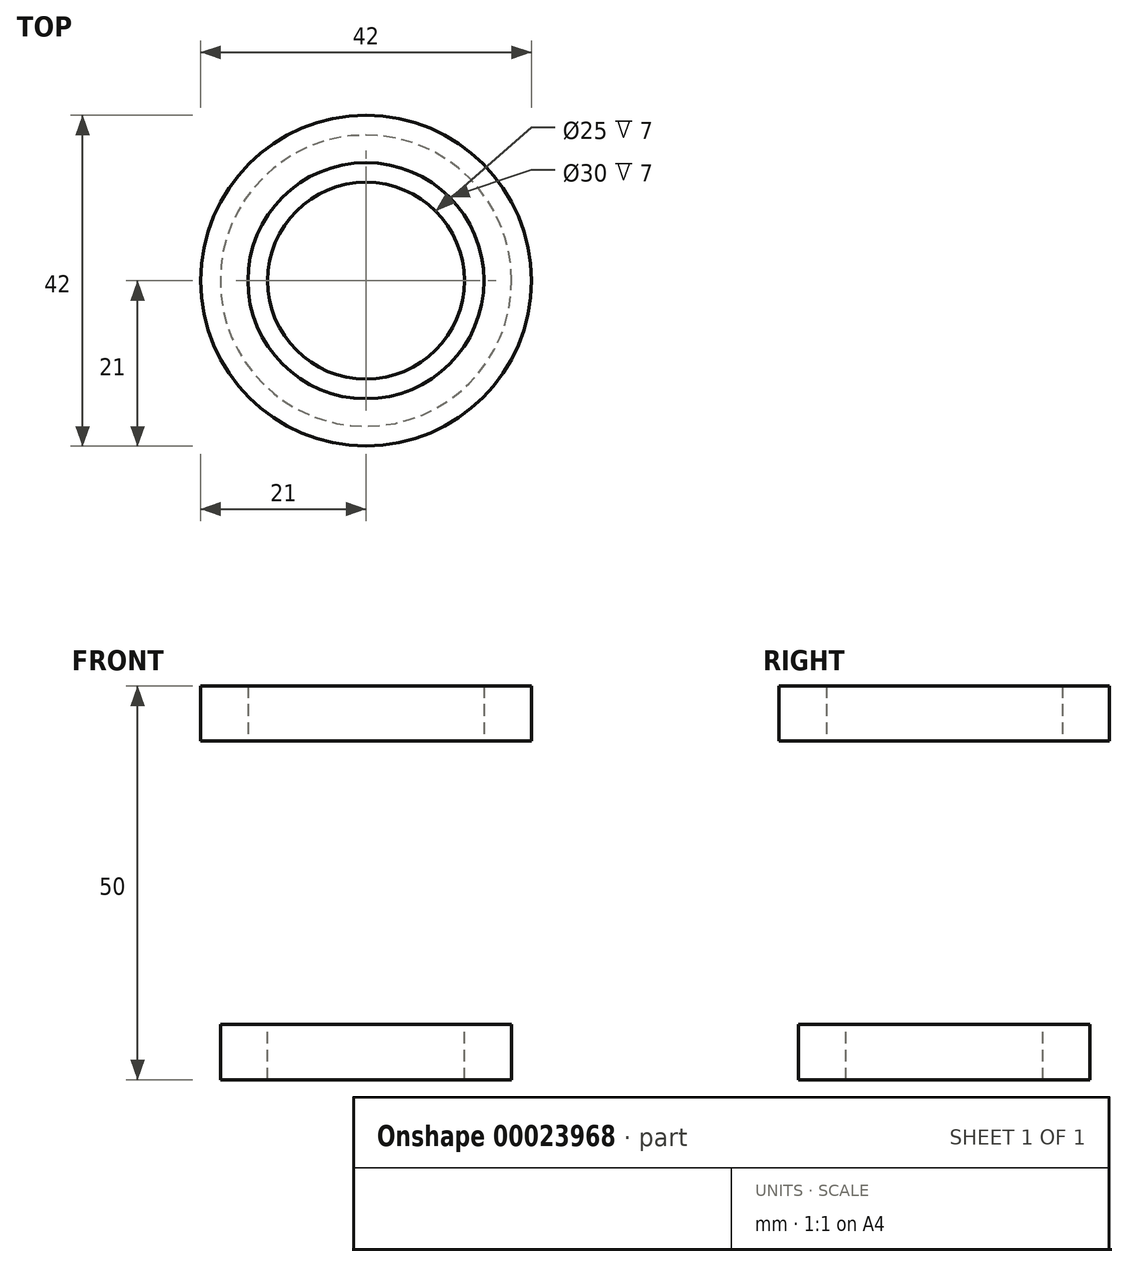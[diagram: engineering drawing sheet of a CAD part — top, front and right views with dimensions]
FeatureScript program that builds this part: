
annotation { "Feature Type Name" : "Feature", "Feature Type Description" : "" }
export const myFeature = defineFeature(function(context is Context, id is Id, definition is map)
    precondition{}
    {
        {
            var Q0;
            Q0=qCreatedBy(makeId("Front.planeOp"),FACE);
            var sketch = newSketch(context, id + "F0", { "sketchPlane" : qUnion([Q0])});
            skLineSegment(sketch, "E0.bottom", {"start": v(-21, 40) * mm, "end": v(-15, 40) * mm});
            skLineSegment(sketch, "E0.top", {"start": v(-21, 33) * mm, "end": v(-15, 33) * mm});
            skLineSegment(sketch, "E0.left", {"start": v(-21, 40) * mm, "end": v(-21, 33) * mm});
            skLineSegment(sketch, "E0.right", {"start": v(-15, 40) * mm, "end": v(-15, 33) * mm});
            skLineSegment(sketch, "E1", {"start": v(0, 0) * mm, "end": v(0, 29.3) * mm, "construction": true});
            skSolve(sketch);
        }
        {
            var Q0;
            Q0 = qSketchRegion(id + "F0", true);
            var Q1;
            Q1=sQuery(id+"F0.wireOp",EDGE,"E1");
            revolve(context, id + "F1", {"entities" : qUnion([Q0]), "axis" : qUnion([Q1]), "revolveType" : RevolveType.FULL});
        }
        {
            var Q0;
            Q0=qCreatedBy(makeId("Front.planeOp"),FACE);
            var sketch = newSketch(context, id + "F2", { "sketchPlane" : qUnion([Q0])});
            skLineSegment(sketch, "E2.bottom", {"start": v(-18.5, -3) * mm, "end": v(-12.5, -3) * mm});
            skLineSegment(sketch, "E2.top", {"start": v(-18.5, -10) * mm, "end": v(-12.5, -10) * mm});
            skLineSegment(sketch, "E2.left", {"start": v(-18.5, -3) * mm, "end": v(-18.5, -10) * mm});
            skLineSegment(sketch, "E2.right", {"start": v(-12.5, -3) * mm, "end": v(-12.5, -10) * mm});
            skLineSegment(sketch, "E3", {"start": v(0, 0) * mm, "end": v(0, -6.26) * mm, "construction": true});
            skSolve(sketch);
        }
        {
            var Q0;
            Q0=makeQuery(id+"F2.imprint","IMPRINT",FACE,{"disambiguationData":[TD([[makeQuery(id+"F2.imprint","IMPRINT",EDGE,{"derivedFrom":sQuery(id+"F2.wireOp",EDGE,"E2.bottom")}),-1.0]])]});
            var Q1;
            Q1=sQuery(id+"F2.wireOp",EDGE,"E3");
            revolve(context, id + "F3", {"entities" : qUnion([Q0]), "axis" : qUnion([Q1]), "revolveType" : RevolveType.FULL});
        }
        {
            var Q0;
            Q0=qCreatedBy(makeId("Front.planeOp"),FACE);
            var sketch = newSketch(context, id + "F4", { "sketchPlane" : qUnion([Q0])});
            skLineSegment(sketch, "E4", {"start": v(-21, 40) * mm, "end": v(-18.5, -10) * mm});
            skLineSegment(sketch, "E5", {"start": v(-18.5, -10) * mm, "end": v(-315, -10) * mm});
            skLineSegment(sketch, "E6", {"start": v(-315, -10) * mm, "end": v(-315, -8.92) * mm});
            skLineSegment(sketch, "E7", {"start": v(-315, 10) * mm, "end": v(-21, 40) * mm});
            skArc(sketch, "E8", {"start": v(-315, -8.92) * mm, "mid": v(-311.37, 0) * mm, "end": v(-315, 8.92) * mm});
            skLineSegment(sketch, "E9.trimOffspring", {"start": v(-315, 8.92) * mm, "end": v(-315, 10) * mm});
            skLineSegment(sketch, "E10", {"start": v(0, 0) * mm, "end": v(0, 20.16) * mm, "construction": true});
            skSolve(sketch);
        }
        {
            var Q0;
            Q0 = qConstructionFilter(qBodyType(qCreatedBy(id + "F4" ,EDGE), BodyType.WIRE), ConstructionObject.NO);
            var Q1;
            Q1=sQuery(id+"F4.wireOp",EDGE,"E10");
            revolve(context, id + "F5", {"bodyType" : ToolBodyType.SURFACE, "surfaceEntities" : qUnion([Q0]), "axis" : qUnion([Q1]), "revolveType" : RevolveType.FULL});
        }
        {
            var Q0;
            Q0=makeQuery(id+"F5.opRevolve","SWEPT_FACE",FACE,{"disambiguationData":[OSD([sQuery(id+"F4.wireOp",EDGE,"E5")])]});
            var sketch = newSketch(context, id + "F6", { "sketchPlane" : qUnion([Q0])});
            skCircle(sketch, "E11", {"center": v(0, 184.15) * mm, "radius": 10 * mm});
            skSolve(sketch);
        }
        {
            var Q0;
            Q0 = qSketchRegion(id + "F6", true);
            var Q1;
            Q1=makeQuery(id+"F5.opRevolve","SWEPT_FACE",FACE,{"disambiguationData":[OSD([sQuery(id+"F4.wireOp",EDGE,"E7")])]});
            extrude(context, id + "F7", {"entities" : qUnion([Q0]), "operationType" : NewBodyOperationType.REMOVE, "oppositeDirection" : true, "depth" : 3 * mm, "hasSecondDirection" : true, "secondDirectionBound" : SecondDirectionBoundingType.UP_TO_SURFACE, "secondDirectionOppositeDirection" : false, "secondDirectionBoundEntityFace" : qUnion([Q1]), "secondDirectionDepth" : 25 * mm});
        }
    });
